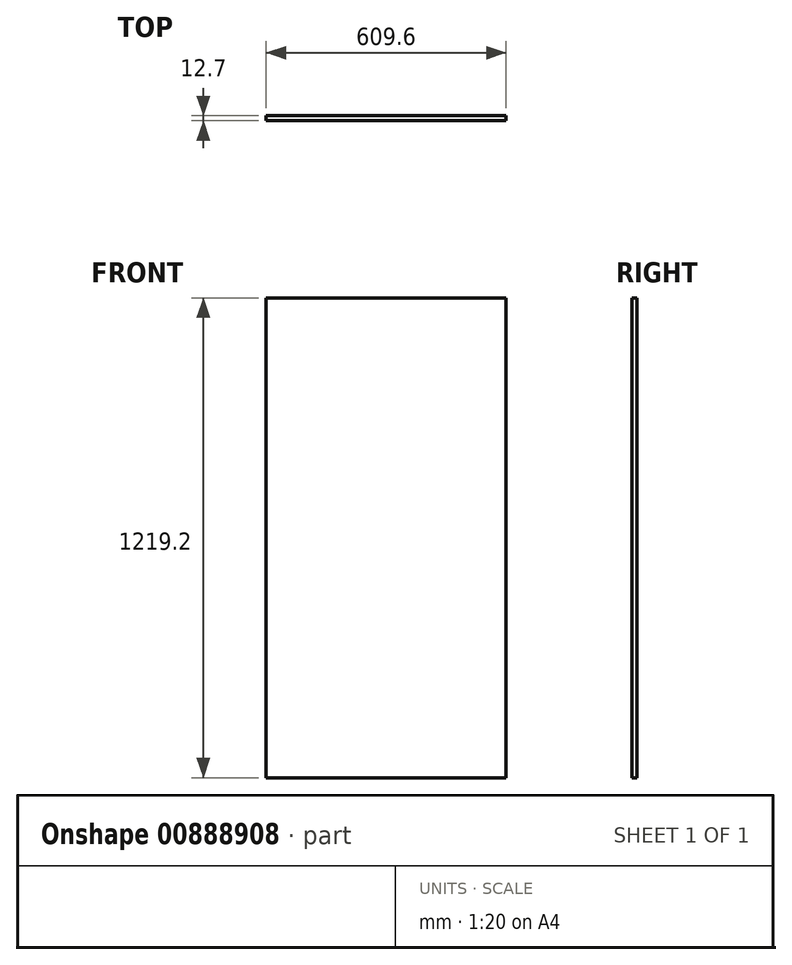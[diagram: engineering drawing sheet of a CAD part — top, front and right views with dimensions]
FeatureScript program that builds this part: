
annotation { "Feature Type Name" : "Feature", "Feature Type Description" : "" }
export const myFeature = defineFeature(function(context is Context, id is Id, definition is map)
    precondition{}
    {
        {
            var Q0;
            Q0=qCreatedBy(makeId("Front.planeOp"),FACE);
            var sketch = newSketch(context, id + "F0", { "sketchPlane" : qUnion([Q0])});
            skLineSegment(sketch, "E0.bottom", {"start": v(0, 0) * mm, "end": v(609.6, 0) * mm});
            skLineSegment(sketch, "E0.top", {"start": v(0, 1219.2) * mm, "end": v(609.6, 1219.2) * mm});
            skLineSegment(sketch, "E0.left", {"start": v(0, 0) * mm, "end": v(0, 1219.2) * mm});
            skLineSegment(sketch, "E0.right", {"start": v(609.6, 0) * mm, "end": v(609.6, 1219.2) * mm});
            skSolve(sketch);
        }
        {
            var Q0;
            Q0=makeQuery(id+"F0.imprint","IMPRINT",FACE,{"disambiguationData":[TD([[makeQuery(id+"F0.imprint","IMPRINT",EDGE,{"derivedFrom":sQuery(id+"F0.wireOp",EDGE,"E0.bottom")}),1.0]])]});
            extrude(context, id + "F1", {"entities" : qUnion([Q0]), "depth" : 12.7 * mm, "offsetDistance" : 25.4 * mm});
        }
    });
